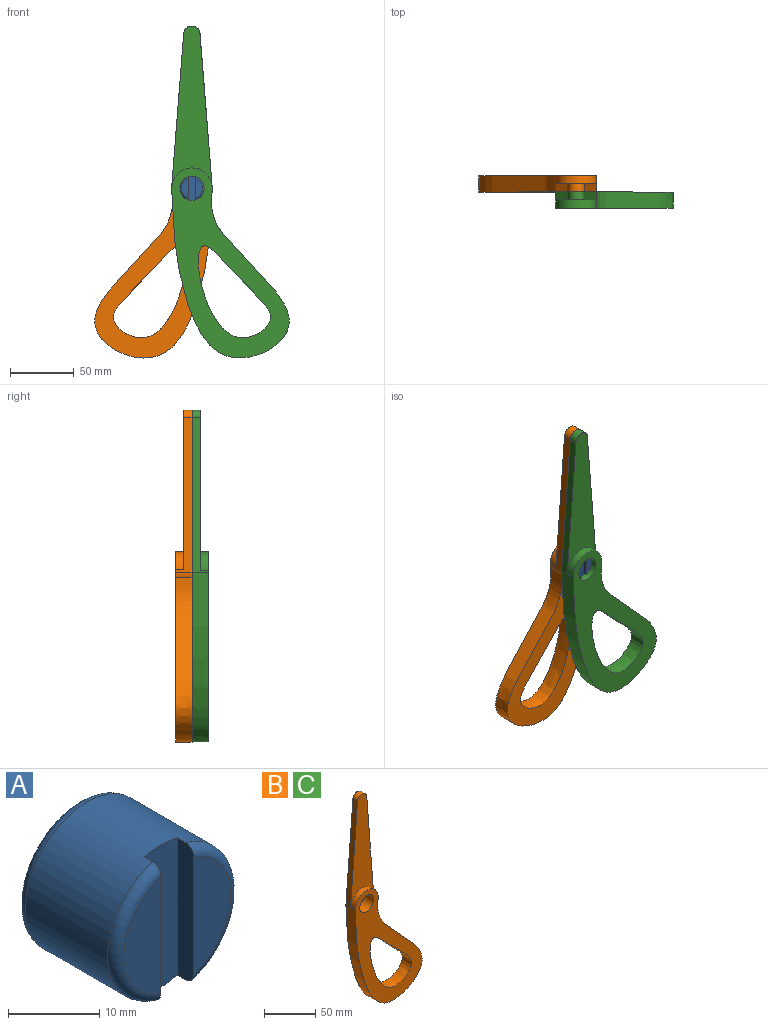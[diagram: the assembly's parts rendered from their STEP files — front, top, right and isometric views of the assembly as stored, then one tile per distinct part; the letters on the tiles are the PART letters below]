
ASSEMBLY  parts=3 mates=3
PART A: 10 faces, bbox 20.6x15.2x20.6 mm
  f0: plane 15.71x5.72mm, normal (0,-1,0), area 65.8mm2, adj f5,f9
  f1: cylinder r=9.53mm len=19.05mm, axis (0,1,0), area 747mm2, adj f4,f5,f6,f7,f8,f9
  f2: plane 15.71x5.72mm, normal (0,-1,0), area 65.8mm2, adj f4,f7
  f3: plane 16.51x16.51mm, normal (0,1,0), area 214.1mm2, adj f8
  f4: plane 18.36x2.54mm, normal (1,0,0), area 45.9mm2, adj f1,f2,f6,f7
  f5: plane 18.36x2.54mm, normal (-1,0,0), area 45.9mm2, adj f0,f1,f6,f9
  f6: plane 19.05x5.08mm, normal (0,-1,0), area 95.6mm2, adj f1,f4,f5
  f7: torus R=8.26mm, axis (0,-1,0), area 46.5mm2, adj f1,f2,f4
  f8: torus R=8.26mm, axis (0,-1,0), area 113.6mm2, adj f1,f3
  f9: torus R=8.26mm, axis (0,-1,0), area 46.5mm2, adj f0,f1,f5
PART B: 11 faces, bbox 95.9x12.7x263.8 mm
  f0: plane 125.75x31.5mm, normal (0,-1,0), area 2354.4mm2, adj f1,f2,f4,f8
  f1: cylinder r=6.35mm len=12.66mm, axis (0,1,0), area 120.3mm2, adj f0,f2,f4,f6
  f2: plane 121.15x12.7mm, normal (-1,0,0.08), area 779.7mm2, adj f0,f1,f6,f7,f8,f10
  f3: cylinder r=15.88mm len=12.7mm, axis (0,1,0), area 54.9mm2, adj f4,f6,f7,f10
  f4: plane 121.15x12.7mm, normal (1,0,0.08), area 787.5mm2, adj f0,f1,f3,f6,f8,f10
  f5: cylinder r=9.53mm len=19.05mm, axis (0,1,0), area 760.1mm2, adj f6,f10
  f6: plane 263.83x95.87mm, normal (0,1,0), area 7221.1mm2, adj f1,f2,f3,f4,f5,f7,f9
  f7: extruded ~132.74x91.99mm, area 4171.3mm2, adj f2,f3,f6,f10
  f8: cylinder r=15.88mm len=31.5mm, axis (0,1,0), area 292.9mm2, adj f0,f2,f4,f10
  f9: extruded ~71.89x56.46mm, area 2488.4mm2, adj f6,f10
  f10: plane 152.7x95.87mm, normal (0,-1,0), area 4866.7mm2, adj f2,f3,f4,f5,f7,f8,f9
PART C: same geometry as B
PLACE A t=(-133.09,-78.14,-25.75)mm
PLACE B rot(axis=(0,0,-1),180deg) t=(-133.09,-84.49,-25.75)mm fixed
PLACE C rot(axis=(0,-1,0),0.1deg) t=(-133.09,-84.49,-25.75)mm
MATE revolute A.f1 <-> C.f8  axis (0,-1,0) through (-133.09,-90.84,-25.75)mm
MATE parallel C.f6 <-> B.f6  axis (0,1,0) through (-118.81,-84.49,-50.63)mm
MATE revolute B.f5 <-> C.f5  axis (0,-1,0) through (-133.09,-84.49,-25.75)mm
